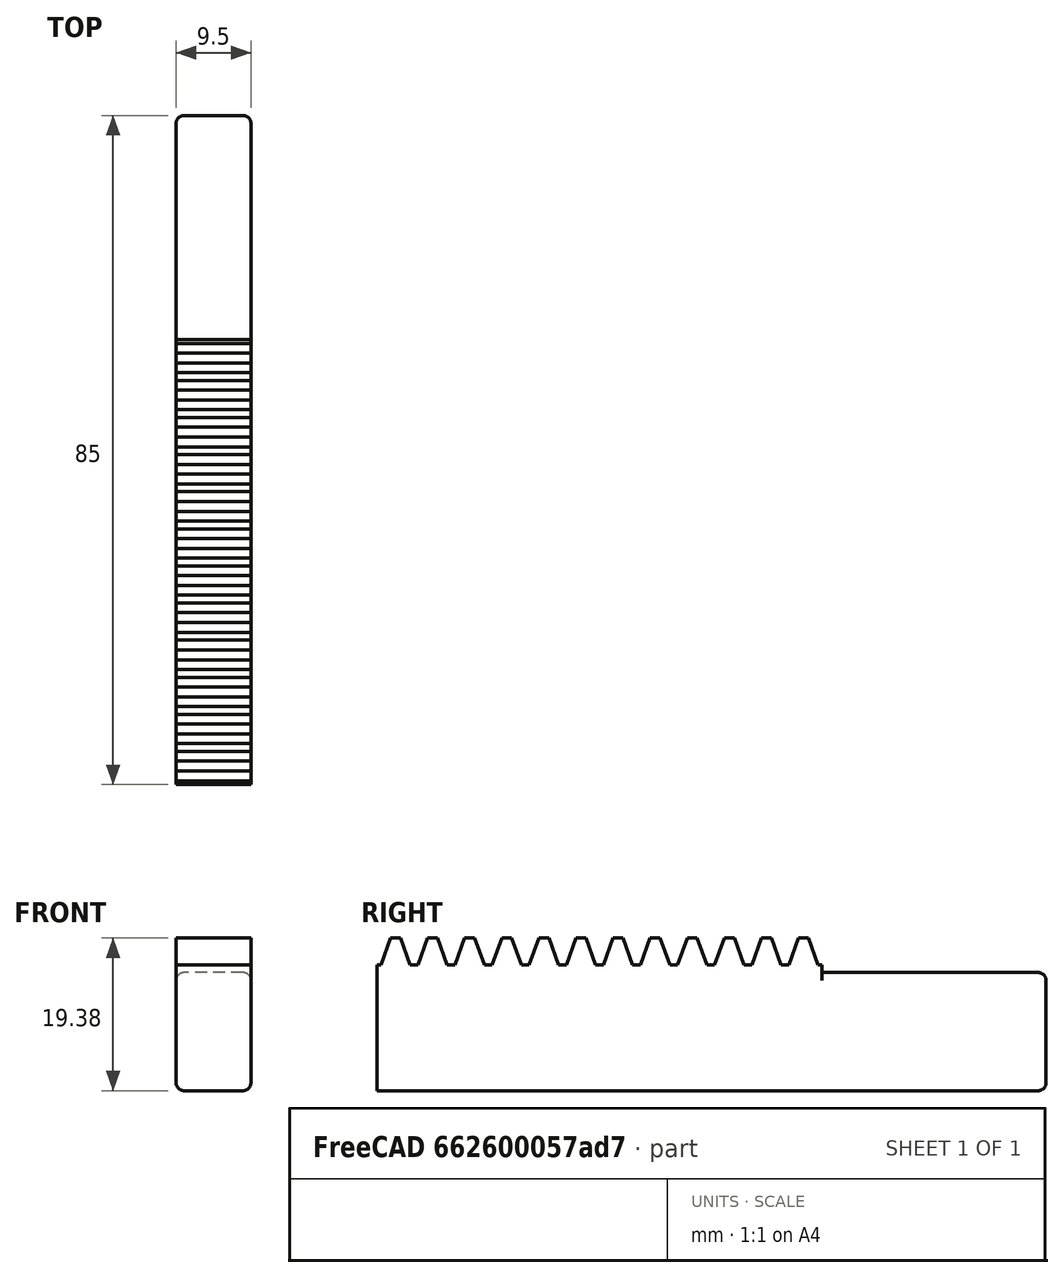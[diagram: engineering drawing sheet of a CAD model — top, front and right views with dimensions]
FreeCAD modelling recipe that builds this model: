
FCSTD DOCUMENT  (FreeCAD 0.18R16146 (Git))
Label: rack
License: Creative Commons Attribution-ShareAlike
LicenseURL: http://creativecommons.org/licenses/by-sa/4.0/
objects: Part::FeaturePython×1, Part::Box×1, Part::MultiFuse×1, Part::Fillet×1
note: 4 computed .brp shape members not serialized (recipe doc carries the construction recipe); baked Part::Feature solids carry a one-line shape summary decoded from their .brp

FEATURE [Part::FeaturePython] InvoluteRack  # WARN: FeaturePython — macro-defined, semantics opaque (R4)
  Placement = pos=(9.5,2.35619,17.875) rot=(0,-1,0;1.5708rad)
  add_endings = true
  beta = 0
  clearence = 0.25
  double_helix = false
  head = 0
  height = 9.5
  module = 1.5
  pressure_angle = 20
  properties_from_tool = true
  simplified = false
  teeth = 12
  thickness = 1
  transverse_pitch = 4.71239
FEATURE [Part::Box] Box  label="Cube"
  AttacherType = Attacher::AttachEngine3D
  Height = 15
  Length = 9.5
  Width = 85
FEATURE [Part::MultiFuse] Fusion
  Refine = true
  Shapes = -> [Box,InvoluteRack]
FEATURE [Part::Fillet] Fillet
  Base = -> Fusion
  Edges = 8 edges r=1: [Edge152,Edge153,Edge154,Edge155,Edge156,Edge157,Edge158,Edge159]
